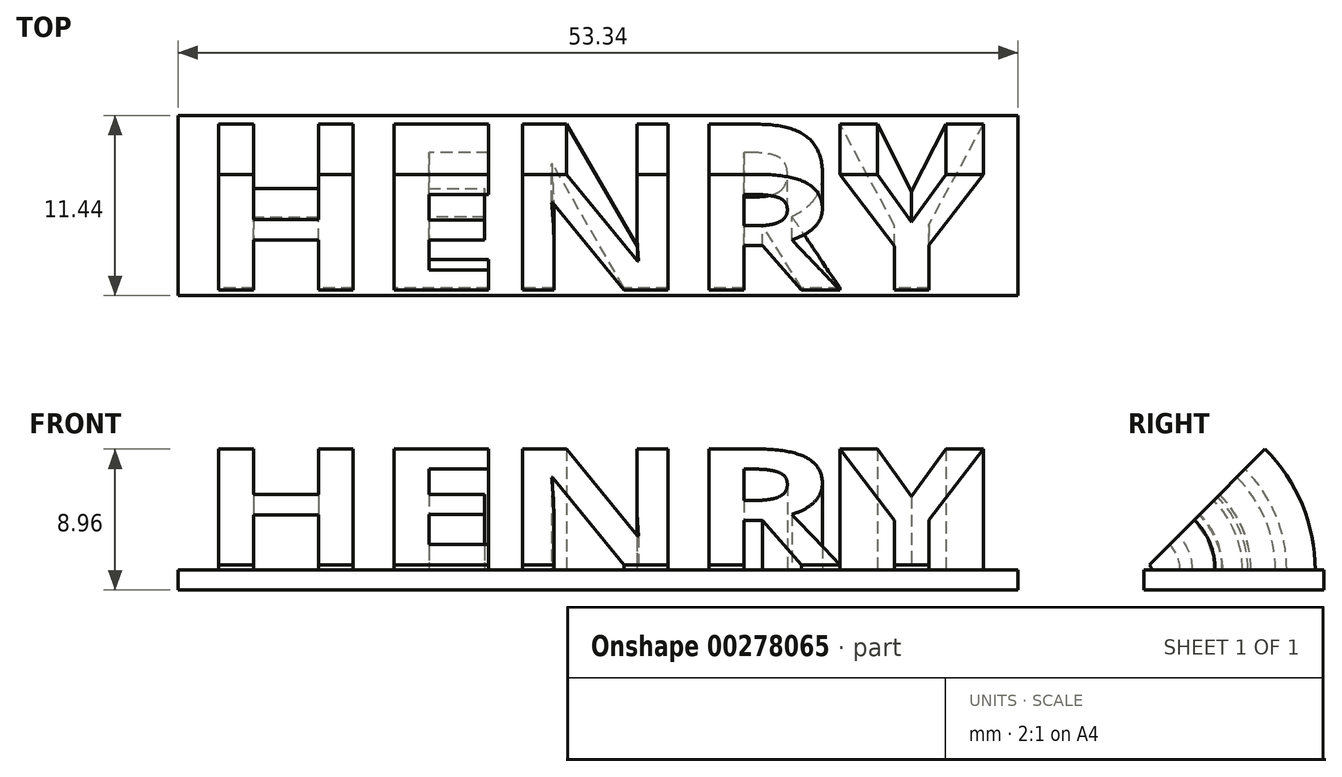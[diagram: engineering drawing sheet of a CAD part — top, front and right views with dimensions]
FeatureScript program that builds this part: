
annotation { "Feature Type Name" : "Feature", "Feature Type Description" : "" }
export const myFeature = defineFeature(function(context is Context, id is Id, definition is map)
    precondition{}
    {
        {
            var Q0;
            Q0=qCreatedBy(makeId("Top.planeOp"),FACE);
            var sketch = newSketch(context, id + "F0", { "sketchPlane" : qUnion([Q0])});
            skText(sketch, "E0", { "text": "HENRY", "fontName": "OpenSans-Bold.ttf"});
            skLineSegment(sketch, "E1.bottom", {"start": v(26.67, -5.71) * mm, "end": v(-26.67, -5.72) * mm});
            skLineSegment(sketch, "E1.top", {"start": v(26.67, 5.72) * mm, "end": v(-26.67, 5.71) * mm});
            skLineSegment(sketch, "E1.left", {"start": v(26.67, -5.71) * mm, "end": v(26.67, 5.72) * mm});
            skLineSegment(sketch, "E1.right", {"start": v(-26.67, -5.72) * mm, "end": v(-26.67, 5.71) * mm});
            skPoint(sketch, "E1.middle", {"position": v(0, 0) * mm});
            const initialGuessF0  = {"E0": [-0.0254, -0.00524, 1, 0, 0.01049]};
            skSetInitialGuess(sketch, initialGuessF0);
            skSolve(sketch);
        }
        {
            var Q0;
            Q0=makeQuery(id+"F0.imprint","IMPRINT",FACE,{"disambiguationData":[TD([[makeQuery(id+"F0.imprint","IMPRINT",EDGE,{"derivedFrom":sQuery(id+"F0.wireOp",EDGE,"E0.sketch_text.stroke-0")}),1.0]])]});
            var Q1;
            Q1=makeQuery(id+"F0.imprint","IMPRINT",FACE,{"disambiguationData":[TD([[makeQuery(id+"F0.imprint","IMPRINT",EDGE,{"derivedFrom":sQuery(id+"F0.wireOp",EDGE,"E0.sketch_text.stroke-0")}),-1.0]])]});
            var Q2;
            Q2=makeQuery(id+"F0.imprint","IMPRINT",FACE,{"disambiguationData":[TD([[makeQuery(id+"F0.imprint","IMPRINT",EDGE,{"derivedFrom":sQuery(id+"F0.wireOp",EDGE,"E0.sketch_text.stroke-12")}),-1.0]])]});
            var Q3;
            Q3=makeQuery(id+"F0.imprint","IMPRINT",FACE,{"disambiguationData":[TD([[makeQuery(id+"F0.imprint","IMPRINT",EDGE,{"derivedFrom":sQuery(id+"F0.wireOp",EDGE,"E0.sketch_text.stroke-24")}),-1.0]])]});
            var Q4;
            Q4=makeQuery(id+"F0.imprint","IMPRINT",FACE,{"disambiguationData":[TD([[makeQuery(id+"F0.imprint","IMPRINT",EDGE,{"derivedFrom":sQuery(id+"F0.wireOp",EDGE,"E0.sketch_text.stroke-38")}),-1.0]])]});
            var Q5;
            Q5=makeQuery(id+"F0.imprint","IMPRINT",FACE,{"disambiguationData":[TD([[makeQuery(id+"F0.imprint","IMPRINT",EDGE,{"derivedFrom":sQuery(id+"F0.wireOp",EDGE,"E0.sketch_text.stroke-38")}),1.0]])]});
            var Q6;
            Q6=makeQuery(id+"F0.imprint","IMPRINT",FACE,{"disambiguationData":[TD([[makeQuery(id+"F0.imprint","IMPRINT",EDGE,{"derivedFrom":sQuery(id+"F0.wireOp",EDGE,"E0.sketch_text.stroke-57")}),-1.0]])]});
            extrude(context, id + "F1", {"entities" : qUnion([Q0, Q1, Q2, Q3, Q4, Q5, Q6]), "oppositeDirection" : true, "depth" : 1.27 * mm});
        }
        {
            var Q0;
            Q0=makeQuery(id+"F0.imprint","IMPRINT",FACE,{"disambiguationData":[TD([[makeQuery(id+"F0.imprint","IMPRINT",EDGE,{"derivedFrom":sQuery(id+"F0.wireOp",EDGE,"E0.sketch_text.stroke-0")}),-1.0]])]});
            var Q1;
            Q1=makeQuery(id+"F0.imprint","IMPRINT",FACE,{"disambiguationData":[TD([[makeQuery(id+"F0.imprint","IMPRINT",EDGE,{"derivedFrom":sQuery(id+"F0.wireOp",EDGE,"E0.sketch_text.stroke-12")}),-1.0]])]});
            var Q2;
            Q2=makeQuery(id+"F0.imprint","IMPRINT",FACE,{"disambiguationData":[TD([[makeQuery(id+"F0.imprint","IMPRINT",EDGE,{"derivedFrom":sQuery(id+"F0.wireOp",EDGE,"E0.sketch_text.stroke-24")}),-1.0]])]});
            var Q3;
            Q3=makeQuery(id+"F0.imprint","IMPRINT",FACE,{"disambiguationData":[TD([[makeQuery(id+"F0.imprint","IMPRINT",EDGE,{"derivedFrom":sQuery(id+"F0.wireOp",EDGE,"E0.sketch_text.stroke-38")}),-1.0]])]});
            var Q4;
            Q4=makeQuery(id+"F0.imprint","IMPRINT",FACE,{"disambiguationData":[TD([[makeQuery(id+"F0.imprint","IMPRINT",EDGE,{"derivedFrom":sQuery(id+"F0.wireOp",EDGE,"E0.sketch_text.stroke-57")}),-1.0]])]});
            var Q5;
            Q5=sQuery(id+"F0.wireOp",EDGE,"E1.bottom");
            revolve(context, id + "F2", {"operationType" : NewBodyOperationType.ADD, "entities" : qUnion([Q0, Q1, Q2, Q3, Q4]), "axis" : qUnion([Q5]), "revolveType" : RevolveType.ONE_DIRECTION, "oppositeDirection" : true, "angle" : 45 * degree});
        }
    });
